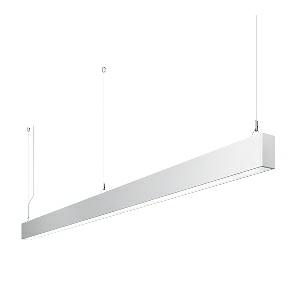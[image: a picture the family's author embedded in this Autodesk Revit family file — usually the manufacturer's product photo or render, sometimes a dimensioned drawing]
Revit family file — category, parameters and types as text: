
# Revit family: idoo_line_-_ilp_6000_830_d_00805744_3d5b
name_source: partatom
category: Lighting Fixtures
units: mm (PartAtom-declared; Revit-internal decimal feet)

## family parameters
Cut with Voids When Loaded = No
Host = Face
Light Source = No
Part Type = Normal
Room Calculation Point = No
Round Connector Dimension = Use Diameter
Shared = No

## types (1)
- IDOO.line - ILP 6000/830/D (1 x LED, 6000 lm, 3000K)
    Apparent Load = 46 VA
    Approval mark = CE
    CIE Flux Codes = 66 91 98 40 100
    Color Rendering = 80-89
    Color Temperature = 3000K
    Control Gear = Electronic ballast
    Default Elevation = 1800 mm
    Description = ILP 6000/830/D|Suspended luminaire|light source: LED|connected load: 220-240V, 50/60Hz|Power consumption: approx. 46 W|standby: approx. 0,15|luminous flux: 6000 lm|luminous efficacy: 130 lm/W|light distribution: Direct/indirect|direct ratio: approx. 40 %|colour temperature: Warm white, ca. 3000 K|color rendering index (CRI): >= 80|chromaticity tolerance:  3 SDCM|System of protection: IP 40|technology: Continuously dimmable|luminaire body|material: Sectional aluminium|colour: White|lamp cover: Acrylic (PMMA), Clear|mains lead: 2.00 m With free stranded wires|Fastening: Steel cable 0.3 - 0.7 m|glare control: Prism aperture|luminance(L65): <= 2700 cd/m|unified glare rating(4H 8H): <=  16|special features: DALI Load 1x, TouchDIM - dimming via standard switch, Flicker-free, Suitable as emergency lighting|
    Frequency = 50 Hz
    Height = 110 mm
    Lamp = 1 x LED
    Lamp Light Flux = 6000 lm
    Lamp count = 1
    Length = 2256 mm
    Luminous efficacy = 130 lm/W
    Manufacturer = Waldmann
    ModVariant = No
    Model = 00805744
    Mounting Place = Ceiling
    Mounting Type = Pendant
    Number of Poles = 1
    OnlyDefault = Yes
    Power Factor = 1
    Product Name = IDOO.line - ILP 6000/830/D
    Product group = Suspended luminaire
    ProductGroupID = 9
    Protection Class = Protection class I
    Protection Degree = IP 40
    RLX_Detail_Level = 1
    RLX_Emergency_Light_Flux = 0 lm
    RLX_Emergency_Type = 0
    RLX_Emergency_Type_DB = No
    RlxData = <blob elided: 21149 chars, md5=b812bc3a>
    Socket = socket
    Standby Power = 0 W
    System Light Flux = 6000 lm
    System Power = 46 W
    Type Comments = Product without accessories
    Type Image = 113293000-00692530.jpg
    URL = http://relux.com
    VarID = ---
    Voltage = 230 V
    Voltage Range = 220-240 V
    Weight = 0.00 kg
    Width = 60 mm  [stored 0.19685 ft]

note: [stored X ft] marks values corroborated as IEEE doubles in the binary element streams (Revit-internal decimal feet)

## geometry (parser evidence)
native form markers: Blend x4, Sweep x14
no freeform markers — native parametric forms only
